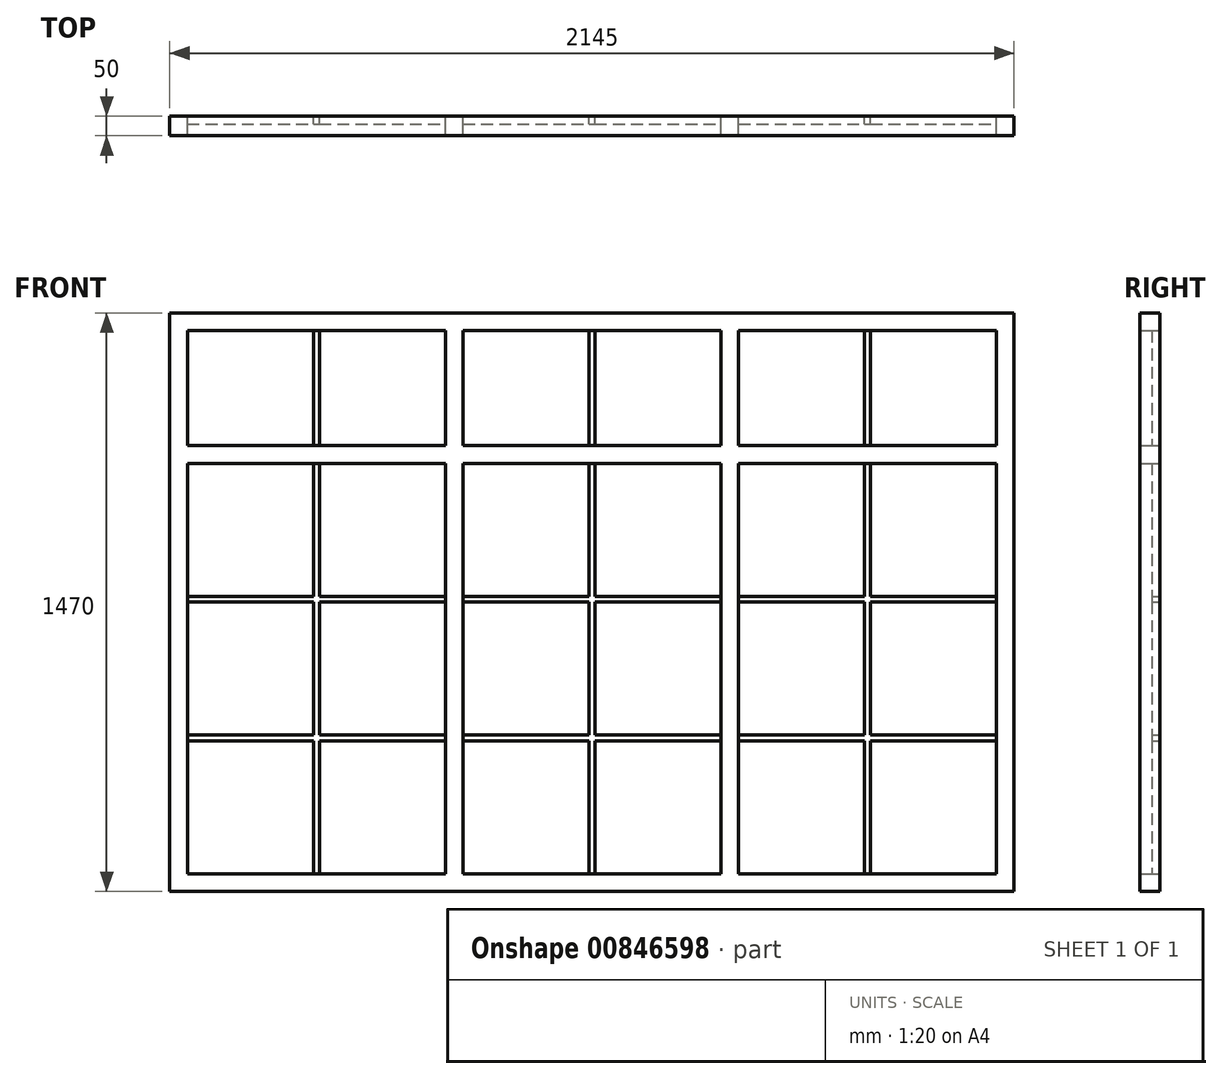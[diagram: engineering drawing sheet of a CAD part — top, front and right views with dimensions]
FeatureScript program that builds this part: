
annotation { "Feature Type Name" : "Feature", "Feature Type Description" : "" }
export const myFeature = defineFeature(function(context is Context, id is Id, definition is map)
    precondition{}
    {
        {
            var Q0;
            Q0=qCreatedBy(makeId("Front.planeOp"),FACE);
            var sketch = newSketch(context, id + "F0", { "sketchPlane" : qUnion([Q0])});
            skLineSegment(sketch, "E0.bottom", {"start": v(0, 0) * mm, "end": v(2145, 0) * mm});
            skLineSegment(sketch, "E0.top", {"start": v(0, 1470) * mm, "end": v(2145, 1470) * mm});
            skLineSegment(sketch, "E0.left", {"start": v(0, 0) * mm, "end": v(0, 1470) * mm});
            skLineSegment(sketch, "E0.right", {"start": v(2145, 0) * mm, "end": v(2145, 1470) * mm});
            skLineSegment(sketch, "E1.bottom", {"start": v(45, 1425) * mm, "end": v(700, 1425) * mm});
            skLineSegment(sketch, "E1.top", {"start": v(45, 45) * mm, "end": v(700, 45) * mm});
            skLineSegment(sketch, "E1.left", {"start": v(45, 1425) * mm, "end": v(45, 1132.5) * mm});
            skLineSegment(sketch, "E1.right", {"start": v(700, 1425) * mm, "end": v(700, 1132.5) * mm});
            skLineSegment(sketch, "E2.bottom", {"start": v(745, 1425) * mm, "end": v(1400, 1425) * mm});
            skLineSegment(sketch, "E2.top", {"start": v(745, 1132.5) * mm, "end": v(1400, 1132.5) * mm});
            skLineSegment(sketch, "E2.left", {"start": v(745, 1425) * mm, "end": v(745, 1132.5) * mm});
            skLineSegment(sketch, "E2.right", {"start": v(1400, 1425) * mm, "end": v(1400, 1132.5) * mm});
            skLineSegment(sketch, "E3.bottom", {"start": v(745, 1087.5) * mm, "end": v(1400, 1087.5) * mm});
            skLineSegment(sketch, "E3.top", {"start": v(745, 45) * mm, "end": v(1400, 45) * mm});
            skLineSegment(sketch, "E3.left", {"start": v(745, 1087.5) * mm, "end": v(745, 45) * mm});
            skLineSegment(sketch, "E3.right", {"start": v(1400, 1087.5) * mm, "end": v(1400, 45) * mm});
            skLineSegment(sketch, "E4.bottom", {"start": v(1445, 1425) * mm, "end": v(2100, 1425) * mm});
            skLineSegment(sketch, "E4.top", {"start": v(1445, 45) * mm, "end": v(2100, 45) * mm});
            skLineSegment(sketch, "E4.left", {"start": v(1445, 1425) * mm, "end": v(1445, 1132.5) * mm});
            skLineSegment(sketch, "E4.right", {"start": v(2100, 1425) * mm, "end": v(2100, 1132.5) * mm});
            skLineSegment(sketch, "E5.bottom", {"start": v(45, 1132.5) * mm, "end": v(700, 1132.5) * mm});
            skLineSegment(sketch, "E5.top", {"start": v(45, 1087.5) * mm, "end": v(700, 1087.5) * mm});
            skLineSegment(sketch, "E6.trimOffspring", {"start": v(45, 1087.5) * mm, "end": v(45, 45) * mm});
            skLineSegment(sketch, "E7.trimOffspring", {"start": v(700, 1087.5) * mm, "end": v(700, 45) * mm});
            skLineSegment(sketch, "E8.bottom", {"start": v(1445, 1132.5) * mm, "end": v(2100, 1132.5) * mm});
            skLineSegment(sketch, "E8.top", {"start": v(1445, 1087.5) * mm, "end": v(2100, 1087.5) * mm});
            skLineSegment(sketch, "E9.trimOffspring", {"start": v(1445, 1087.5) * mm, "end": v(1445, 45) * mm});
            skLineSegment(sketch, "E10.trimOffspring", {"start": v(2100, 1087.5) * mm, "end": v(2100, 45) * mm});
            skSolve(sketch);
        }
        {
            var Q0;
            Q0=qSketchRegion(id+"F0",true);
            extrude(context, id + "F1", {"entities" : qUnion([Q0]), "depth" : 50 * mm, "offsetDistance" : 25 * mm});
        }
        {
            var Q0;
            Q0=qCreatedBy(makeId("Front.planeOp"),FACE);
            var sketch = newSketch(context, id + "F2", { "sketchPlane" : qUnion([Q0])});
            skLineSegment(sketch, "E11.bottom", {"start": v(45, 750) * mm, "end": v(365, 750) * mm});
            skLineSegment(sketch, "E11.top", {"start": v(45, 735) * mm, "end": v(365, 735) * mm});
            skLineSegment(sketch, "E11.left", {"start": v(45, 750) * mm, "end": v(45, 735) * mm});
            skLineSegment(sketch, "E11.right", {"start": v(700, 750) * mm, "end": v(700, 735) * mm});
            skLineSegment(sketch, "E12.bottom", {"start": v(45, 397.5) * mm, "end": v(365, 397.5) * mm});
            skLineSegment(sketch, "E12.top", {"start": v(45, 382.5) * mm, "end": v(365, 382.5) * mm});
            skLineSegment(sketch, "E12.left", {"start": v(45, 397.5) * mm, "end": v(45, 382.5) * mm});
            skLineSegment(sketch, "E12.right", {"start": v(700, 397.5) * mm, "end": v(700, 382.5) * mm});
            skLineSegment(sketch, "E13.bottom", {"start": v(365, 1087.5) * mm, "end": v(380, 1087.5) * mm});
            skLineSegment(sketch, "E13.top", {"start": v(365, 45) * mm, "end": v(380, 45) * mm});
            skLineSegment(sketch, "E13.left", {"start": v(365, 1087.5) * mm, "end": v(365, 750) * mm});
            skLineSegment(sketch, "E13.right", {"start": v(380, 1087.5) * mm, "end": v(380, 750) * mm});
            skLineSegment(sketch, "E14.bottom", {"start": v(365, 1425) * mm, "end": v(380, 1425) * mm});
            skLineSegment(sketch, "E14.top", {"start": v(365, 1132.5) * mm, "end": v(380, 1132.5) * mm});
            skLineSegment(sketch, "E14.left", {"start": v(365, 1425) * mm, "end": v(365, 1132.5) * mm});
            skLineSegment(sketch, "E14.right", {"start": v(380, 1425) * mm, "end": v(380, 1132.5) * mm});
            skLineSegment(sketch, "E15.bottom", {"start": v(1065, 1425) * mm, "end": v(1080, 1425) * mm});
            skLineSegment(sketch, "E15.top", {"start": v(1065, 1132.5) * mm, "end": v(1080, 1132.5) * mm});
            skLineSegment(sketch, "E15.left", {"start": v(1065, 1425) * mm, "end": v(1065, 1132.5) * mm});
            skLineSegment(sketch, "E15.right", {"start": v(1080, 1425) * mm, "end": v(1080, 1132.5) * mm});
            skLineSegment(sketch, "E16.bottom", {"start": v(745, 750) * mm, "end": v(1065, 750) * mm});
            skLineSegment(sketch, "E16.top", {"start": v(745, 735) * mm, "end": v(1065, 735) * mm});
            skLineSegment(sketch, "E16.left", {"start": v(745, 750) * mm, "end": v(745, 735) * mm});
            skLineSegment(sketch, "E16.right", {"start": v(1400, 750) * mm, "end": v(1400, 735) * mm});
            skLineSegment(sketch, "E17.bottom", {"start": v(745, 397.5) * mm, "end": v(1065, 397.5) * mm});
            skLineSegment(sketch, "E17.top", {"start": v(745, 382.5) * mm, "end": v(1065, 382.5) * mm});
            skLineSegment(sketch, "E17.left", {"start": v(745, 397.5) * mm, "end": v(745, 382.5) * mm});
            skLineSegment(sketch, "E17.right", {"start": v(1400, 397.5) * mm, "end": v(1400, 382.5) * mm});
            skLineSegment(sketch, "E18.bottom", {"start": v(1065, 1087.5) * mm, "end": v(1080, 1087.5) * mm});
            skLineSegment(sketch, "E18.top", {"start": v(1065, 45) * mm, "end": v(1080, 45) * mm});
            skLineSegment(sketch, "E18.left", {"start": v(1065, 1087.5) * mm, "end": v(1065, 750) * mm});
            skLineSegment(sketch, "E18.right", {"start": v(1080, 1087.5) * mm, "end": v(1080, 750) * mm});
            skLineSegment(sketch, "E19.bottom", {"start": v(1765, 1425) * mm, "end": v(1780, 1425) * mm});
            skLineSegment(sketch, "E19.top", {"start": v(1765, 1132.5) * mm, "end": v(1780, 1132.5) * mm});
            skLineSegment(sketch, "E19.left", {"start": v(1780, 1425) * mm, "end": v(1780, 1132.5) * mm});
            skLineSegment(sketch, "E19.right", {"start": v(1765, 1425) * mm, "end": v(1765, 1132.5) * mm});
            skLineSegment(sketch, "E20.bottom", {"start": v(1765, 1087.5) * mm, "end": v(1780, 1087.5) * mm});
            skLineSegment(sketch, "E20.top", {"start": v(1765, 45) * mm, "end": v(1780, 45) * mm});
            skLineSegment(sketch, "E20.left", {"start": v(1765, 1087.5) * mm, "end": v(1765, 750) * mm});
            skLineSegment(sketch, "E20.right", {"start": v(1780, 1087.5) * mm, "end": v(1780, 750) * mm});
            skLineSegment(sketch, "E21.bottom", {"start": v(1445, 735) * mm, "end": v(1765, 735) * mm});
            skLineSegment(sketch, "E21.top", {"start": v(1445, 750) * mm, "end": v(1765, 750) * mm});
            skLineSegment(sketch, "E21.left", {"start": v(1445, 750) * mm, "end": v(1445, 735) * mm});
            skLineSegment(sketch, "E21.right", {"start": v(2100, 750) * mm, "end": v(2100, 735) * mm});
            skLineSegment(sketch, "E22.bottom", {"start": v(1445, 397.5) * mm, "end": v(1765, 397.5) * mm});
            skLineSegment(sketch, "E22.top", {"start": v(1445, 382.5) * mm, "end": v(1765, 382.5) * mm});
            skLineSegment(sketch, "E22.left", {"start": v(1445, 397.5) * mm, "end": v(1445, 382.5) * mm});
            skLineSegment(sketch, "E22.right", {"start": v(2100, 397.5) * mm, "end": v(2100, 382.5) * mm});
            skLineSegment(sketch, "E23.trimOffspring", {"start": v(380, 750) * mm, "end": v(700, 750) * mm});
            skLineSegment(sketch, "E24.trimOffspring", {"start": v(365, 735) * mm, "end": v(365, 397.5) * mm});
            skLineSegment(sketch, "E25.trimOffspring", {"start": v(380, 735) * mm, "end": v(700, 735) * mm});
            skLineSegment(sketch, "E26.trimOffspring", {"start": v(380, 735) * mm, "end": v(380, 397.5) * mm});
            skLineSegment(sketch, "E27.trimOffspring", {"start": v(380, 397.5) * mm, "end": v(700, 397.5) * mm});
            skLineSegment(sketch, "E28.trimOffspring", {"start": v(365, 382.5) * mm, "end": v(365, 45) * mm});
            skLineSegment(sketch, "E29.trimOffspring", {"start": v(380, 382.5) * mm, "end": v(700, 382.5) * mm});
            skLineSegment(sketch, "E30.trimOffspring", {"start": v(380, 382.5) * mm, "end": v(380, 45) * mm});
            skLineSegment(sketch, "E31.trimOffspring", {"start": v(1080, 750) * mm, "end": v(1400, 750) * mm});
            skLineSegment(sketch, "E32.trimOffspring", {"start": v(1065, 735) * mm, "end": v(1065, 397.5) * mm});
            skLineSegment(sketch, "E33.trimOffspring", {"start": v(1080, 735) * mm, "end": v(1400, 735) * mm});
            skLineSegment(sketch, "E34.trimOffspring", {"start": v(1080, 735) * mm, "end": v(1080, 397.5) * mm});
            skLineSegment(sketch, "E35.trimOffspring", {"start": v(1765, 735) * mm, "end": v(1765, 397.5) * mm});
            skLineSegment(sketch, "E36.trimOffspring", {"start": v(1780, 750) * mm, "end": v(2100, 750) * mm});
            skLineSegment(sketch, "E37.trimOffspring", {"start": v(1780, 735) * mm, "end": v(1780, 397.5) * mm});
            skLineSegment(sketch, "E38.trimOffspring", {"start": v(1780, 735) * mm, "end": v(2100, 735) * mm});
            skLineSegment(sketch, "E39.trimOffspring", {"start": v(1065, 382.5) * mm, "end": v(1065, 45) * mm});
            skLineSegment(sketch, "E40.trimOffspring", {"start": v(1080, 397.5) * mm, "end": v(1400, 397.5) * mm});
            skLineSegment(sketch, "E41.trimOffspring", {"start": v(1080, 382.5) * mm, "end": v(1080, 45) * mm});
            skLineSegment(sketch, "E42.trimOffspring", {"start": v(1080, 382.5) * mm, "end": v(1400, 382.5) * mm});
            skLineSegment(sketch, "E43.trimOffspring", {"start": v(1765, 382.5) * mm, "end": v(1765, 45) * mm});
            skLineSegment(sketch, "E44.trimOffspring", {"start": v(1780, 382.5) * mm, "end": v(1780, 45) * mm});
            skLineSegment(sketch, "E45.trimOffspring", {"start": v(1780, 397.5) * mm, "end": v(2100, 397.5) * mm});
            skLineSegment(sketch, "E46.trimOffspring", {"start": v(1780, 382.5) * mm, "end": v(2100, 382.5) * mm});
            skSolve(sketch);
        }
        {
            var Q0;
            Q0 = qSketchRegion(id + "F2", true);
            extrude(context, id + "F3", {"entities" : qUnion([Q0]), "operationType" : NewBodyOperationType.ADD, "depth" : 20 * mm, "offsetDistance" : 25 * mm});
        }
    });
